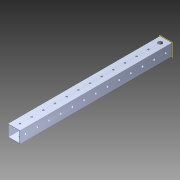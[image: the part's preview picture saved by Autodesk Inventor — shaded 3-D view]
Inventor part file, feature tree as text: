
AUTODESK INVENTOR PART (.ipt)
format: ipt  version: 2014 (Build 180170000, 170)  size: 1,231,872 bytes
history: native  units: in
note: dims shown in document units (in); Inventor stores cm internally (conversion verified against a paired STEP export)
features: extrude x2, sketch x2, pattern_circular x1, other x1, plane x1, imported_body x1
ambient origin geometry x8: Origin, YZ Plane, XZ Plane, XY Plane, X Axis, Y Axis, Z Axis, Center Point
bodies: Body1 (feature_tree)
feature tree (8):
  pattern_circular  "CirPattern2"
  other  "217-3426-STEP1"
  plane  "Work Plane1"
  extrude  "Extrusion1"  Depth=3937.0079in TaperAngle=0.0deg
  extrude  "Extrusion2"  Depth=3.937in TaperAngle=0.0deg
  imported_body  "Base1"
  sketch  "Sketch1"  dims[d0=-13.0in d1=3937.0079in d2=0.0in]
  sketch  "Sketch3"  dims[d3=0.375in d4=3.937in d5=0.0in]
